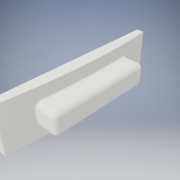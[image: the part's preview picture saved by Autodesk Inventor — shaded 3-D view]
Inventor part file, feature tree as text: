
AUTODESK INVENTOR PART (.ipt)
format: ipt  version: 2019 (Build 230136000, 136)  size: 250,880 bytes
history: native  units: in
note: dims shown in document units (in); Inventor stores cm internally (conversion verified against a paired STEP export)
features: fillet x6, sketch x4, extrude x3, projected_geometry x2
ambient origin geometry x8: Origin, YZ Plane, XZ Plane, XY Plane, X Axis, Y Axis, Z Axis, Center Point
bodies: Body1 (feature_tree)
feature tree (15):
  extrude  "Extrusion2"  Depth=7.4803in
  sketch  "Sketch4"  dims[d11=3.937in d12=1.1811in d13=0.0in]
  extrude  "Extrusion3"  Depth=1.1811in TaperAngle=0.0deg
  extrude  "Extrusion4"  Depth=0.5512in
  fillet  "Fillet1"  Radius=3.937in
  fillet  "Fillet3"  Radius=0.7283in
  fillet  "Fillet6"  Radius=1.1811in
  fillet  "Fillet7"  Radius=0.5512in
  fillet  "Fillet8"  Radius=0.315in
  fillet  "Fillet9"  Radius=0.5906in
  sketch  "Sketch3"  dims[d9=15.3543in d10=7.4803in]
  sketch  "Sketch5"  dims[d14=2.4803in d15=0.5512in d16=3.937in d17=0.7283in d18=1.1811in d19=0.5512in d20=0.315in d21=0.5906in d22=0.0in]
  projected_geometry  "Projected Loop2"
  sketch  "Sketch6"  dims[d23=0.125in d26=0.0394in d29=0.0162in d30=0.1969in d31=0.0in d32=0.0394in d33=0.0394in d34=0.0394in]
  projected_geometry  "Projected Loop3"
